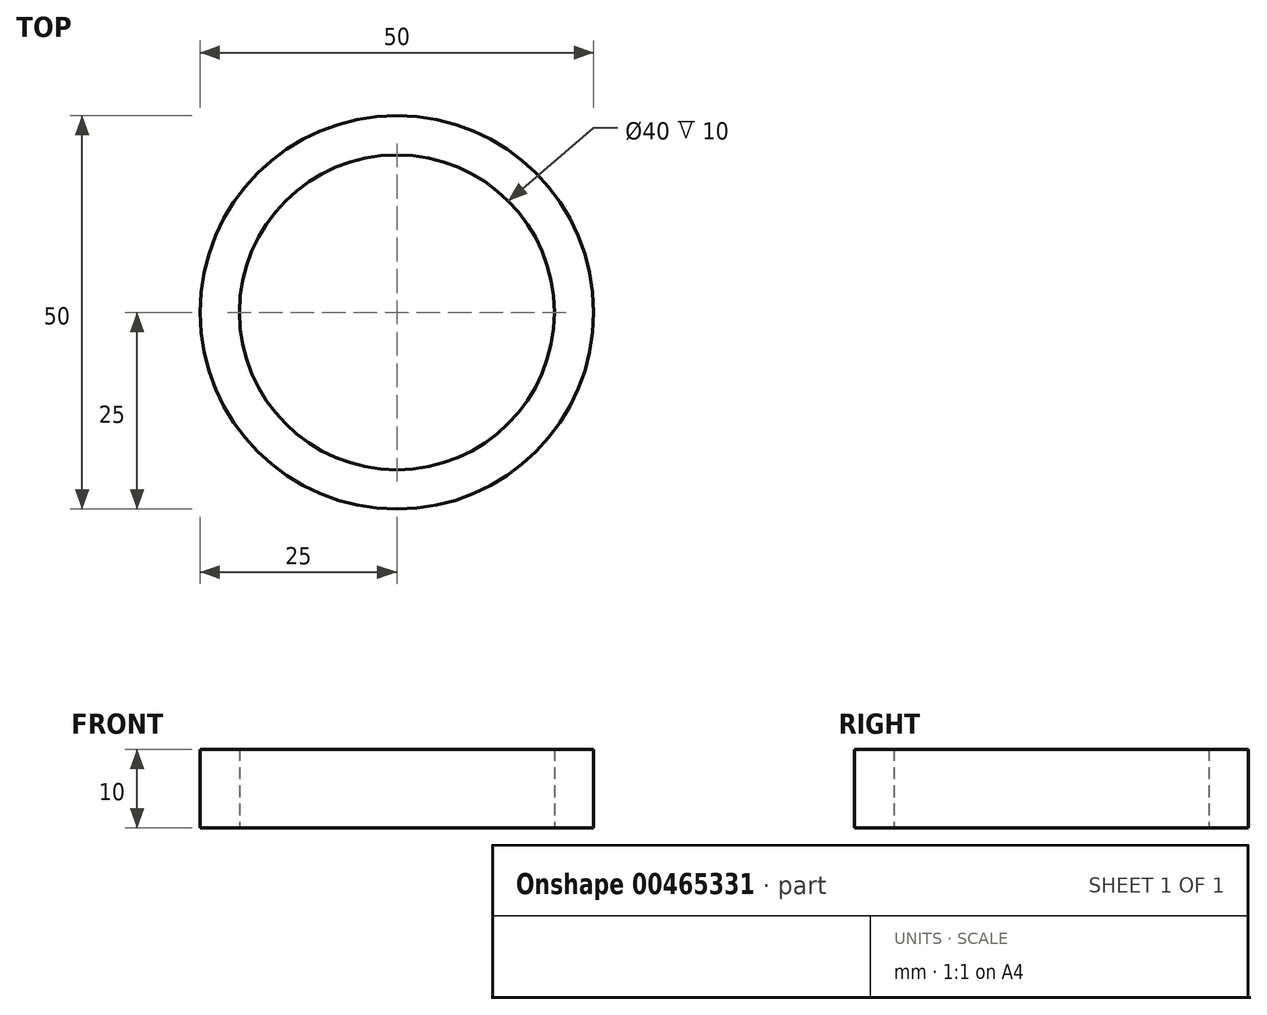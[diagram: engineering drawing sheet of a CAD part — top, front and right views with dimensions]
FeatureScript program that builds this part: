
annotation { "Feature Type Name" : "Feature", "Feature Type Description" : "" }
export const myFeature = defineFeature(function(context is Context, id is Id, definition is map)
    precondition{}
    {
        {
            var Q0;
            Q0=qCreatedBy(makeId("Top.planeOp"),FACE);
            var sketch = newSketch(context, id + "F0", { "sketchPlane" : qUnion([Q0])});
            skCircle(sketch, "E0", {"center": v(0, 0) * mm, "radius": 25 * mm});
            skCircle(sketch, "E1", {"center": v(0, 0) * mm, "radius": 20 * mm});
            skSolve(sketch);
        }
        {
            var Q0;
            Q0 = qSketchRegion(id + "F0", true);
            extrude(context, id + "F1", {"entities" : qUnion([Q0]), "depth" : 10 * mm});
        }
    });
